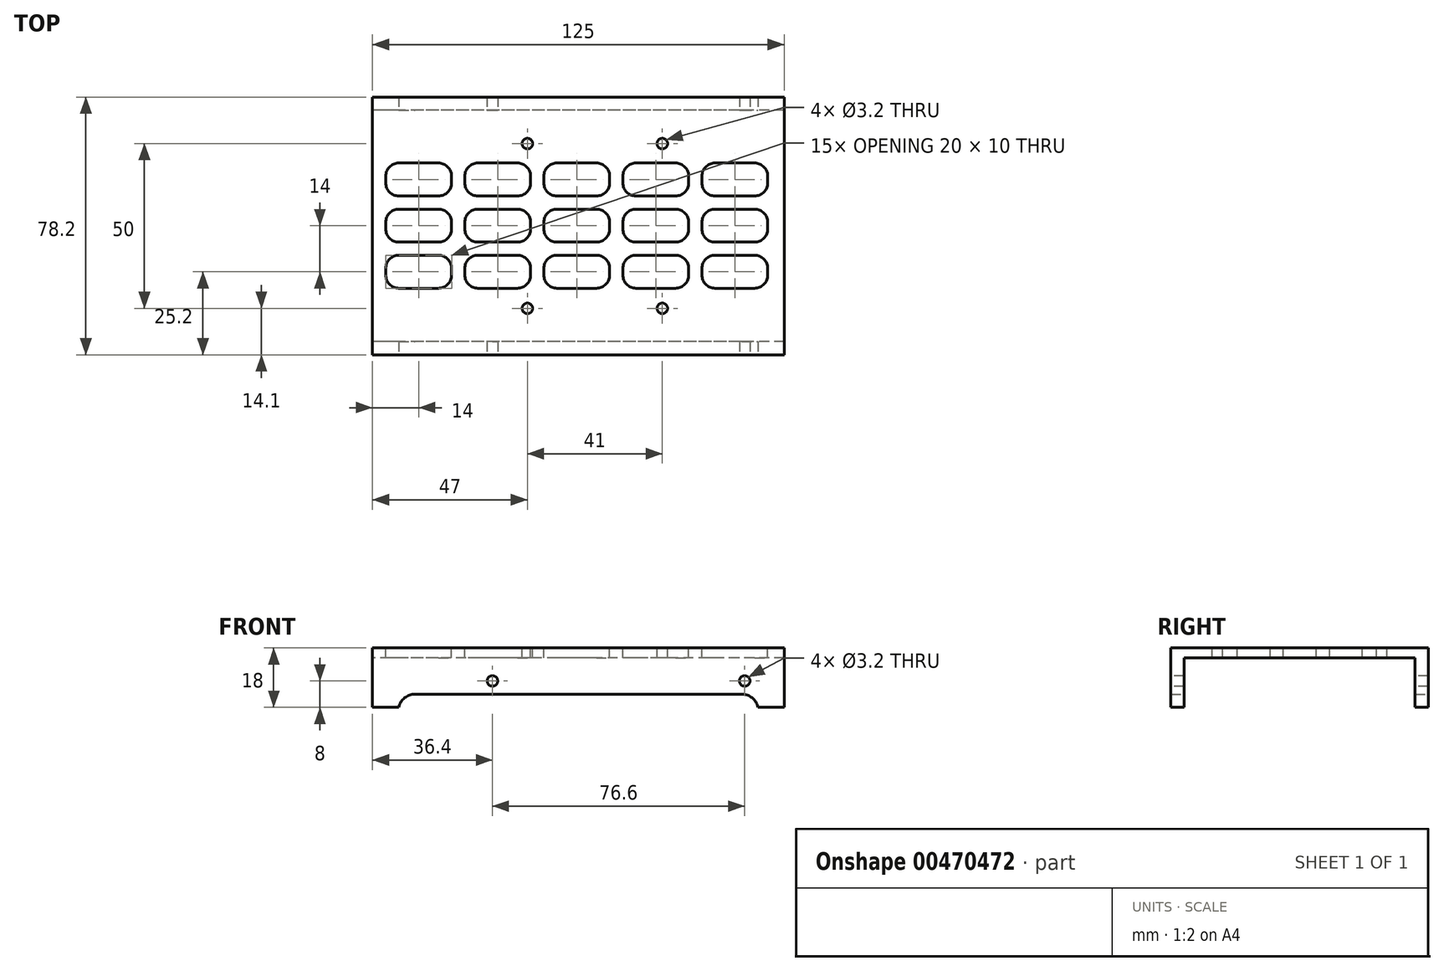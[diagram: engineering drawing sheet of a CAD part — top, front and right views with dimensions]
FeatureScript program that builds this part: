
annotation { "Feature Type Name" : "Feature", "Feature Type Description" : "" }
export const myFeature = defineFeature(function(context is Context, id is Id, definition is map)
    precondition{}
    {
        {
            var Q0;
            Q0=qCreatedBy(makeId("Top.planeOp"),FACE);
            var sketch = newSketch(context, id + "F0", { "sketchPlane" : qUnion([Q0])});
            skLineSegment(sketch, "E0.bottom", {"start": v(0, 0) * mm, "end": v(125, 0) * mm});
            skLineSegment(sketch, "E0.top", {"start": v(0, 78.2) * mm, "end": v(125, 78.2) * mm});
            skLineSegment(sketch, "E0.left", {"start": v(0, 0) * mm, "end": v(0, 78.2) * mm});
            skLineSegment(sketch, "E0.right", {"start": v(125, 0) * mm, "end": v(125, 78.2) * mm});
            skSolve(sketch);
        }
        {
            var Q0;
            Q0 = qSketchRegion(id + "F0", true);
            extrude(context, id + "F1", {"entities" : qUnion([Q0]), "depth" : 3 * mm});
        }
        {
            var Q0;
            Q0=makeQuery(id+"F1.opExtrude","CAP_FACE",FACE,{"disambiguationData":[OSD([sQuery(id+"F0.wireOp",EDGE,"E0.bottom"),sQuery(id+"F0.wireOp",EDGE,"E0.top"),sQuery(id+"F0.wireOp",EDGE,"E0.left"),sQuery(id+"F0.wireOp",EDGE,"E0.right")])],"isStart":true});
            var sketch = newSketch(context, id + "F2", { "sketchPlane" : qUnion([Q0])});
            skLineSegment(sketch, "E1.bottom", {"start": v(125, -78.2) * mm, "end": v(0, -78.2) * mm});
            skLineSegment(sketch, "E1.top", {"start": v(125, -74.2) * mm, "end": v(0, -74.2) * mm});
            skLineSegment(sketch, "E1.left", {"start": v(125, -78.2) * mm, "end": v(125, -74.2) * mm});
            skLineSegment(sketch, "E1.right", {"start": v(0, -78.2) * mm, "end": v(0, -74.2) * mm});
            skLineSegment(sketch, "E2.bottom", {"start": v(125, 0) * mm, "end": v(0, 0) * mm});
            skLineSegment(sketch, "E2.top", {"start": v(125, -4) * mm, "end": v(0, -4) * mm});
            skLineSegment(sketch, "E2.left", {"start": v(125, 0) * mm, "end": v(125, -4) * mm});
            skLineSegment(sketch, "E2.right", {"start": v(0, 0) * mm, "end": v(0, -4) * mm});
            skSolve(sketch);
        }
        {
            var Q0;
            Q0 = qSketchRegion(id + "F2", true);
            extrude(context, id + "F3", {"entities" : qUnion([Q0]), "operationType" : NewBodyOperationType.ADD, "depth" : 15 * mm});
        }
        {
            var Q0;
            Q0=makeQuery(id+"F3.boolean.opBoolean","MERGE",FACE,{"derivedFrom":[makeQuery(id+"F1.opExtrude","SWEPT_FACE",FACE,{"disambiguationData":[OSD([sQuery(id+"F0.wireOp",EDGE,"E0.bottom")])]}),makeQuery(id+"F3.opExtrude","SWEPT_FACE",FACE,{"disambiguationData":[OSD([sQuery(id+"F2.wireOp",EDGE,"E2.bottom")])]})]});
            var sketch = newSketch(context, id + "F4", { "sketchPlane" : qUnion([Q0])});
            skPoint(sketch, "E3", {"position": v(113, -7) * mm});
            skPoint(sketch, "E4.1.0.0", {"position": v(36.4, -7) * mm});
            skLineSegment(sketch, "E4.direction1", {"start": v(113, -7) * mm, "end": v(36.4, -7) * mm, "construction": true});
            skSolve(sketch);
        }
        {
            var Q0;
            Q0=sQuery(id+"F4.wireOp",VERTEX,"E3");
            var Q1;
            Q1=sQuery(id+"F4.wireOp",VERTEX,"E4.1.0.0");
            var Q2;
            Q2=makeQuery(id+"F1.opExtrude","SWEPT_BODY",BODY,{"disambiguationData":[OSD([sQuery(id+"F0.wireOp",EDGE,"E0.bottom"),sQuery(id+"F0.wireOp",EDGE,"E0.top"),sQuery(id+"F0.wireOp",EDGE,"E0.left"),sQuery(id+"F0.wireOp",EDGE,"E0.right")])]});
            hole(context, id + "F5", {"style" : HoleStyle.SIMPLE, "endStyle" : HoleEndStyle.THROUGH, "holeDiameter" : 3.2 * mm, "isTappedThrough" : true, "tappedDepth" : 12 * mm, "tapClearance" : 3, "locations" : qUnion([Q0, Q1]), "scope" : qUnion([Q2])});
        }
        {
            var Q0;
            Q0=makeQuery(id+"F3.boolean.opBoolean","MERGE",FACE,{"derivedFrom":[makeQuery(id+"F1.opExtrude","SWEPT_FACE",FACE,{"disambiguationData":[OSD([sQuery(id+"F0.wireOp",EDGE,"E0.bottom")])]}),makeQuery(id+"F3.opExtrude","SWEPT_FACE",FACE,{"disambiguationData":[OSD([sQuery(id+"F2.wireOp",EDGE,"E2.bottom")])]})]});
            var sketch = newSketch(context, id + "F6", { "sketchPlane" : qUnion([Q0])});
            skLineSegment(sketch, "E5.bottom", {"start": v(8, -11) * mm, "end": v(117, -11) * mm});
            skLineSegment(sketch, "E5.top", {"start": v(8, -15) * mm, "end": v(117, -15) * mm});
            skLineSegment(sketch, "E5.left", {"start": v(8, -11) * mm, "end": v(8, -15) * mm});
            skLineSegment(sketch, "E5.right", {"start": v(117, -11) * mm, "end": v(117, -15) * mm});
            skSolve(sketch);
        }
        {
            var Q0;
            Q0 = qSketchRegion(id + "F6", true);
            extrude(context, id + "F7", {"entities" : qUnion([Q0]), "operationType" : NewBodyOperationType.REMOVE, "endBound" : BoundingType.THROUGH_ALL, "oppositeDirection" : true, "depth" : 25 * mm});
        }
        {
            var Q0;
            Q0=makeQuery(id+"F1.opExtrude","CAP_FACE",FACE,{"disambiguationData":[OSD([sQuery(id+"F0.wireOp",EDGE,"E0.bottom"),sQuery(id+"F0.wireOp",EDGE,"E0.top"),sQuery(id+"F0.wireOp",EDGE,"E0.left"),sQuery(id+"F0.wireOp",EDGE,"E0.right")])],"isStart":false});
            var sketch = newSketch(context, id + "F8", { "sketchPlane" : qUnion([Q0])});
            skPoint(sketch, "E6", {"position": v(47, 64.1) * mm});
            skPoint(sketch, "E7.0.1.0", {"position": v(47, 14.1) * mm});
            skPoint(sketch, "E7.1.0.0", {"position": v(88, 64.1) * mm});
            skPoint(sketch, "E7.1.1.0", {"position": v(88, 14.1) * mm});
            skLineSegment(sketch, "E7.direction1", {"start": v(47, 64.1) * mm, "end": v(88, 64.1) * mm, "construction": true});
            skLineSegment(sketch, "E7.direction2", {"start": v(47, 64.1) * mm, "end": v(47, 14.1) * mm, "construction": true});
            skSolve(sketch);
        }
        {
            var Q0;
            Q0=sQuery(id+"F8.wireOp",VERTEX,"E7.0.1.0");
            var Q1;
            Q1=sQuery(id+"F8.wireOp",VERTEX,"E7.1.1.0");
            var Q2;
            Q2=sQuery(id+"F8.wireOp",VERTEX,"E7.1.0.0");
            var Q3;
            Q3=sQuery(id+"F8.wireOp",VERTEX,"E6");
            var Q4;
            Q4=makeQuery(id+"F1.opExtrude","SWEPT_BODY",BODY,{"disambiguationData":[OSD([sQuery(id+"F0.wireOp",EDGE,"E0.bottom"),sQuery(id+"F0.wireOp",EDGE,"E0.top"),sQuery(id+"F0.wireOp",EDGE,"E0.left"),sQuery(id+"F0.wireOp",EDGE,"E0.right")])]});
            hole(context, id + "F9", {"style" : HoleStyle.SIMPLE, "endStyle" : HoleEndStyle.THROUGH, "holeDiameter" : 3.2 * mm, "isTappedThrough" : true, "tappedDepth" : 12 * mm, "tapClearance" : 3, "locations" : qUnion([Q0, Q1, Q2, Q3]), "scope" : qUnion([Q4])});
        }
        {
            var Q0;
            {var subQ0=sQuery(id+"F6.wireOp",EDGE,"E5.bottom");var subQ1=sQuery(id+"F6.wireOp",EDGE,"E5.right");Q0=makeQuery(id+"F7.boolean.opBoolean","COPY",EDGE,{"disambiguationData":[TD([makeQuery(id+"F1.opExtrude","SWEPT_FACE",FACE,{"disambiguationData":[OSD([sQuery(id+"F0.wireOp",EDGE,"E0.bottom")])]})])],"derivedFrom":makeQuery(id+"F7.opExtrude","SWEPT_EDGE",EDGE,{"disambiguationData":[OSD([subQ0,subQ1])]})});}
            var Q1;
            {var subQ0=sQuery(id+"F6.wireOp",EDGE,"E5.bottom");var subQ1=sQuery(id+"F6.wireOp",EDGE,"E5.right");Q1=makeQuery(id+"F7.boolean.opBoolean","COPY",EDGE,{"disambiguationData":[TD([makeQuery(id+"F1.opExtrude","SWEPT_FACE",FACE,{"disambiguationData":[OSD([sQuery(id+"F0.wireOp",EDGE,"E0.top")])]})])],"derivedFrom":makeQuery(id+"F7.opExtrude","SWEPT_EDGE",EDGE,{"disambiguationData":[OSD([subQ0,subQ1])]})});}
            var Q2;
            {var subQ0=sQuery(id+"F6.wireOp",EDGE,"E5.bottom");var subQ1=sQuery(id+"F6.wireOp",EDGE,"E5.left");Q2=makeQuery(id+"F7.boolean.opBoolean","COPY",EDGE,{"disambiguationData":[TD([makeQuery(id+"F1.opExtrude","SWEPT_FACE",FACE,{"disambiguationData":[OSD([sQuery(id+"F0.wireOp",EDGE,"E0.bottom")])]})])],"derivedFrom":makeQuery(id+"F7.opExtrude","SWEPT_EDGE",EDGE,{"disambiguationData":[OSD([subQ0,subQ1])]})});}
            var Q3;
            {var subQ0=sQuery(id+"F6.wireOp",EDGE,"E5.bottom");var subQ1=sQuery(id+"F6.wireOp",EDGE,"E5.left");Q3=makeQuery(id+"F7.boolean.opBoolean","COPY",EDGE,{"disambiguationData":[TD([makeQuery(id+"F1.opExtrude","SWEPT_FACE",FACE,{"disambiguationData":[OSD([sQuery(id+"F0.wireOp",EDGE,"E0.top")])]})])],"derivedFrom":makeQuery(id+"F7.opExtrude","SWEPT_EDGE",EDGE,{"disambiguationData":[OSD([subQ0,subQ1])]})});}
            fillet(context, id + "F10", {"entities" : qUnion([Q0, Q1, Q2, Q3]), "radius" : 5 * mm, "tangentPropagation" : true, "allowEdgeOverflow" : false});
        }
        {
            var Q0;
            Q0=makeQuery(id+"F1.opExtrude","CAP_FACE",FACE,{"disambiguationData":[OSD([sQuery(id+"F0.wireOp",EDGE,"E0.bottom"),sQuery(id+"F0.wireOp",EDGE,"E0.top"),sQuery(id+"F0.wireOp",EDGE,"E0.left"),sQuery(id+"F0.wireOp",EDGE,"E0.right")])],"isStart":false});
            var sketch = newSketch(context, id + "F11", { "sketchPlane" : qUnion([Q0])});
            skLineSegment(sketch, "E8.bottom", {"start": v(8, 58.2) * mm, "end": v(20, 58.2) * mm});
            skLineSegment(sketch, "E8.top", {"start": v(8, 48.2) * mm, "end": v(20, 48.2) * mm});
            skLineSegment(sketch, "E8.left", {"start": v(4, 54.2) * mm, "end": v(4, 52.2) * mm});
            skLineSegment(sketch, "E8.right", {"start": v(24, 54.2) * mm, "end": v(24, 52.2) * mm});
            skPoint(sketch, "E9.visualSharp", {"position": v(4, 58.2) * mm});
            skArc(sketch, "E9.filletArc", {"start": v(8, 58.2) * mm, "mid": v(5.17, 57.03) * mm, "end": v(4, 54.2) * mm});
            skPoint(sketch, "E10.visualSharp", {"position": v(4, 48.2) * mm});
            skArc(sketch, "E10.filletArc", {"start": v(4, 52.2) * mm, "mid": v(5.17, 49.37) * mm, "end": v(8, 48.2) * mm});
            skPoint(sketch, "E11.visualSharp", {"position": v(24, 58.2) * mm});
            skArc(sketch, "E11.filletArc", {"start": v(24, 54.2) * mm, "mid": v(22.83, 57.03) * mm, "end": v(20, 58.2) * mm});
            skPoint(sketch, "E12.visualSharp", {"position": v(24, 48.2) * mm});
            skArc(sketch, "E12.filletArc", {"start": v(20, 48.2) * mm, "mid": v(22.83, 49.37) * mm, "end": v(24, 52.2) * mm});
            skArc(sketch, "E13.0.1.0", {"start": v(8, 44.2) * mm, "mid": v(5.17, 43.03) * mm, "end": v(4, 40.2) * mm});
            skLineSegment(sketch, "E13.0.1.1", {"start": v(4, 40.2) * mm, "end": v(4, 38.2) * mm});
            skArc(sketch, "E13.0.1.2", {"start": v(4, 38.2) * mm, "mid": v(5.17, 35.37) * mm, "end": v(8, 34.2) * mm});
            skLineSegment(sketch, "E13.0.1.3", {"start": v(8, 34.2) * mm, "end": v(20, 34.2) * mm});
            skArc(sketch, "E13.0.1.4", {"start": v(20, 34.2) * mm, "mid": v(22.83, 35.37) * mm, "end": v(24, 38.2) * mm});
            skLineSegment(sketch, "E13.0.1.5", {"start": v(24, 40.2) * mm, "end": v(24, 38.2) * mm});
            skArc(sketch, "E13.0.1.6", {"start": v(24, 40.2) * mm, "mid": v(22.83, 43.03) * mm, "end": v(20, 44.2) * mm});
            skLineSegment(sketch, "E13.0.1.7", {"start": v(8, 44.2) * mm, "end": v(20, 44.2) * mm});
            skArc(sketch, "E13.0.2.0", {"start": v(8, 30.2) * mm, "mid": v(5.17, 29.03) * mm, "end": v(4, 26.2) * mm});
            skLineSegment(sketch, "E13.0.2.1", {"start": v(4, 26.2) * mm, "end": v(4, 24.2) * mm});
            skArc(sketch, "E13.0.2.2", {"start": v(4, 24.2) * mm, "mid": v(5.17, 21.37) * mm, "end": v(8, 20.2) * mm});
            skLineSegment(sketch, "E13.0.2.3", {"start": v(8, 20.2) * mm, "end": v(20, 20.2) * mm});
            skArc(sketch, "E13.0.2.4", {"start": v(20, 20.2) * mm, "mid": v(22.83, 21.37) * mm, "end": v(24, 24.2) * mm});
            skLineSegment(sketch, "E13.0.2.5", {"start": v(24, 26.2) * mm, "end": v(24, 24.2) * mm});
            skArc(sketch, "E13.0.2.6", {"start": v(24, 26.2) * mm, "mid": v(22.83, 29.03) * mm, "end": v(20, 30.2) * mm});
            skLineSegment(sketch, "E13.0.2.7", {"start": v(8, 30.2) * mm, "end": v(20, 30.2) * mm});
            skArc(sketch, "E13.1.0.0", {"start": v(32, 58.2) * mm, "mid": v(29.17, 57.03) * mm, "end": v(28, 54.2) * mm});
            skLineSegment(sketch, "E13.1.0.1", {"start": v(28, 54.2) * mm, "end": v(28, 52.2) * mm});
            skArc(sketch, "E13.1.0.2", {"start": v(28, 52.2) * mm, "mid": v(29.17, 49.37) * mm, "end": v(32, 48.2) * mm});
            skLineSegment(sketch, "E13.1.0.3", {"start": v(32, 48.2) * mm, "end": v(44, 48.2) * mm});
            skArc(sketch, "E13.1.0.4", {"start": v(44, 48.2) * mm, "mid": v(46.83, 49.37) * mm, "end": v(48, 52.2) * mm});
            skLineSegment(sketch, "E13.1.0.5", {"start": v(48, 54.2) * mm, "end": v(48, 52.2) * mm});
            skArc(sketch, "E13.1.0.6", {"start": v(48, 54.2) * mm, "mid": v(46.83, 57.03) * mm, "end": v(44, 58.2) * mm});
            skLineSegment(sketch, "E13.1.0.7", {"start": v(32, 58.2) * mm, "end": v(44, 58.2) * mm});
            skArc(sketch, "E13.1.1.0", {"start": v(32, 44.2) * mm, "mid": v(29.17, 43.03) * mm, "end": v(28, 40.2) * mm});
            skLineSegment(sketch, "E13.1.1.1", {"start": v(28, 40.2) * mm, "end": v(28, 38.2) * mm});
            skArc(sketch, "E13.1.1.2", {"start": v(28, 38.2) * mm, "mid": v(29.17, 35.37) * mm, "end": v(32, 34.2) * mm});
            skLineSegment(sketch, "E13.1.1.3", {"start": v(32, 34.2) * mm, "end": v(44, 34.2) * mm});
            skArc(sketch, "E13.1.1.4", {"start": v(44, 34.2) * mm, "mid": v(46.83, 35.37) * mm, "end": v(48, 38.2) * mm});
            skLineSegment(sketch, "E13.1.1.5", {"start": v(48, 40.2) * mm, "end": v(48, 38.2) * mm});
            skArc(sketch, "E13.1.1.6", {"start": v(48, 40.2) * mm, "mid": v(46.83, 43.03) * mm, "end": v(44, 44.2) * mm});
            skLineSegment(sketch, "E13.1.1.7", {"start": v(32, 44.2) * mm, "end": v(44, 44.2) * mm});
            skArc(sketch, "E13.1.2.0", {"start": v(32, 30.2) * mm, "mid": v(29.17, 29.03) * mm, "end": v(28, 26.2) * mm});
            skLineSegment(sketch, "E13.1.2.1", {"start": v(28, 26.2) * mm, "end": v(28, 24.2) * mm});
            skArc(sketch, "E13.1.2.2", {"start": v(28, 24.2) * mm, "mid": v(29.17, 21.37) * mm, "end": v(32, 20.2) * mm});
            skLineSegment(sketch, "E13.1.2.3", {"start": v(32, 20.2) * mm, "end": v(44, 20.2) * mm});
            skArc(sketch, "E13.1.2.4", {"start": v(44, 20.2) * mm, "mid": v(46.83, 21.37) * mm, "end": v(48, 24.2) * mm});
            skLineSegment(sketch, "E13.1.2.5", {"start": v(48, 26.2) * mm, "end": v(48, 24.2) * mm});
            skArc(sketch, "E13.1.2.6", {"start": v(48, 26.2) * mm, "mid": v(46.83, 29.03) * mm, "end": v(44, 30.2) * mm});
            skLineSegment(sketch, "E13.1.2.7", {"start": v(32, 30.2) * mm, "end": v(44, 30.2) * mm});
            skArc(sketch, "E13.2.0.0", {"start": v(56, 58.2) * mm, "mid": v(53.17, 57.03) * mm, "end": v(52, 54.2) * mm});
            skLineSegment(sketch, "E13.2.0.1", {"start": v(52, 54.2) * mm, "end": v(52, 52.2) * mm});
            skArc(sketch, "E13.2.0.2", {"start": v(52, 52.2) * mm, "mid": v(53.17, 49.37) * mm, "end": v(56, 48.2) * mm});
            skLineSegment(sketch, "E13.2.0.3", {"start": v(56, 48.2) * mm, "end": v(68, 48.2) * mm});
            skArc(sketch, "E13.2.0.4", {"start": v(68, 48.2) * mm, "mid": v(70.83, 49.37) * mm, "end": v(72, 52.2) * mm});
            skLineSegment(sketch, "E13.2.0.5", {"start": v(72, 54.2) * mm, "end": v(72, 52.2) * mm});
            skArc(sketch, "E13.2.0.6", {"start": v(72, 54.2) * mm, "mid": v(70.83, 57.03) * mm, "end": v(68, 58.2) * mm});
            skLineSegment(sketch, "E13.2.0.7", {"start": v(56, 58.2) * mm, "end": v(68, 58.2) * mm});
            skArc(sketch, "E13.2.1.0", {"start": v(56, 44.2) * mm, "mid": v(53.17, 43.03) * mm, "end": v(52, 40.2) * mm});
            skLineSegment(sketch, "E13.2.1.1", {"start": v(52, 40.2) * mm, "end": v(52, 38.2) * mm});
            skArc(sketch, "E13.2.1.2", {"start": v(52, 38.2) * mm, "mid": v(53.17, 35.37) * mm, "end": v(56, 34.2) * mm});
            skLineSegment(sketch, "E13.2.1.3", {"start": v(56, 34.2) * mm, "end": v(68, 34.2) * mm});
            skArc(sketch, "E13.2.1.4", {"start": v(68, 34.2) * mm, "mid": v(70.83, 35.37) * mm, "end": v(72, 38.2) * mm});
            skLineSegment(sketch, "E13.2.1.5", {"start": v(72, 40.2) * mm, "end": v(72, 38.2) * mm});
            skArc(sketch, "E13.2.1.6", {"start": v(72, 40.2) * mm, "mid": v(70.83, 43.03) * mm, "end": v(68, 44.2) * mm});
            skLineSegment(sketch, "E13.2.1.7", {"start": v(56, 44.2) * mm, "end": v(68, 44.2) * mm});
            skArc(sketch, "E13.2.2.0", {"start": v(56, 30.2) * mm, "mid": v(53.17, 29.03) * mm, "end": v(52, 26.2) * mm});
            skLineSegment(sketch, "E13.2.2.1", {"start": v(52, 26.2) * mm, "end": v(52, 24.2) * mm});
            skArc(sketch, "E13.2.2.2", {"start": v(52, 24.2) * mm, "mid": v(53.17, 21.37) * mm, "end": v(56, 20.2) * mm});
            skLineSegment(sketch, "E13.2.2.3", {"start": v(56, 20.2) * mm, "end": v(68, 20.2) * mm});
            skArc(sketch, "E13.2.2.4", {"start": v(68, 20.2) * mm, "mid": v(70.83, 21.37) * mm, "end": v(72, 24.2) * mm});
            skLineSegment(sketch, "E13.2.2.5", {"start": v(72, 26.2) * mm, "end": v(72, 24.2) * mm});
            skArc(sketch, "E13.2.2.6", {"start": v(72, 26.2) * mm, "mid": v(70.83, 29.03) * mm, "end": v(68, 30.2) * mm});
            skLineSegment(sketch, "E13.2.2.7", {"start": v(56, 30.2) * mm, "end": v(68, 30.2) * mm});
            skLineSegment(sketch, "E13.direction1", {"start": v(8, 48.2) * mm, "end": v(32, 48.2) * mm, "construction": true});
            skLineSegment(sketch, "E13.direction2", {"start": v(8, 48.2) * mm, "end": v(8, 34.2) * mm, "construction": true});
            skArc(sketch, "E14.0.3.0", {"start": v(80, 58.2) * mm, "mid": v(77.17, 57.03) * mm, "end": v(76, 54.2) * mm});
            skLineSegment(sketch, "E14.4.3.0", {"start": v(76, 54.2) * mm, "end": v(76, 52.2) * mm});
            skArc(sketch, "E14.7.3.0", {"start": v(76, 52.2) * mm, "mid": v(77.17, 49.37) * mm, "end": v(80, 48.2) * mm});
            skLineSegment(sketch, "E14.11.3.0", {"start": v(80, 48.2) * mm, "end": v(92, 48.2) * mm});
            skArc(sketch, "E14.14.3.0", {"start": v(92, 48.2) * mm, "mid": v(94.83, 49.37) * mm, "end": v(96, 52.2) * mm});
            skLineSegment(sketch, "E14.18.3.0", {"start": v(96, 54.2) * mm, "end": v(96, 52.2) * mm});
            skArc(sketch, "E14.21.3.0", {"start": v(96, 54.2) * mm, "mid": v(94.83, 57.03) * mm, "end": v(92, 58.2) * mm});
            skLineSegment(sketch, "E14.25.3.0", {"start": v(80, 58.2) * mm, "end": v(92, 58.2) * mm});
            skArc(sketch, "E14.0.3.1", {"start": v(80, 44.2) * mm, "mid": v(77.17, 43.03) * mm, "end": v(76, 40.2) * mm});
            skLineSegment(sketch, "E14.4.3.1", {"start": v(76, 40.2) * mm, "end": v(76, 38.2) * mm});
            skArc(sketch, "E14.7.3.1", {"start": v(76, 38.2) * mm, "mid": v(77.17, 35.37) * mm, "end": v(80, 34.2) * mm});
            skLineSegment(sketch, "E14.11.3.1", {"start": v(80, 34.2) * mm, "end": v(92, 34.2) * mm});
            skArc(sketch, "E14.14.3.1", {"start": v(92, 34.2) * mm, "mid": v(94.83, 35.37) * mm, "end": v(96, 38.2) * mm});
            skLineSegment(sketch, "E14.18.3.1", {"start": v(96, 40.2) * mm, "end": v(96, 38.2) * mm});
            skArc(sketch, "E14.21.3.1", {"start": v(96, 40.2) * mm, "mid": v(94.83, 43.03) * mm, "end": v(92, 44.2) * mm});
            skLineSegment(sketch, "E14.25.3.1", {"start": v(80, 44.2) * mm, "end": v(92, 44.2) * mm});
            skArc(sketch, "E14.0.3.2", {"start": v(80, 30.2) * mm, "mid": v(77.17, 29.03) * mm, "end": v(76, 26.2) * mm});
            skLineSegment(sketch, "E14.4.3.2", {"start": v(76, 26.2) * mm, "end": v(76, 24.2) * mm});
            skArc(sketch, "E14.7.3.2", {"start": v(76, 24.2) * mm, "mid": v(77.17, 21.37) * mm, "end": v(80, 20.2) * mm});
            skLineSegment(sketch, "E14.11.3.2", {"start": v(80, 20.2) * mm, "end": v(92, 20.2) * mm});
            skArc(sketch, "E14.14.3.2", {"start": v(92, 20.2) * mm, "mid": v(94.83, 21.37) * mm, "end": v(96, 24.2) * mm});
            skLineSegment(sketch, "E14.18.3.2", {"start": v(96, 26.2) * mm, "end": v(96, 24.2) * mm});
            skArc(sketch, "E14.21.3.2", {"start": v(96, 26.2) * mm, "mid": v(94.83, 29.03) * mm, "end": v(92, 30.2) * mm});
            skLineSegment(sketch, "E14.25.3.2", {"start": v(80, 30.2) * mm, "end": v(92, 30.2) * mm});
            skArc(sketch, "E14.0.4.0", {"start": v(104, 58.2) * mm, "mid": v(101.17, 57.03) * mm, "end": v(100, 54.2) * mm});
            skLineSegment(sketch, "E14.4.4.0", {"start": v(100, 54.2) * mm, "end": v(100, 52.2) * mm});
            skArc(sketch, "E14.7.4.0", {"start": v(100, 52.2) * mm, "mid": v(101.17, 49.37) * mm, "end": v(104, 48.2) * mm});
            skLineSegment(sketch, "E14.11.4.0", {"start": v(104, 48.2) * mm, "end": v(116, 48.2) * mm});
            skArc(sketch, "E14.14.4.0", {"start": v(116, 48.2) * mm, "mid": v(118.83, 49.37) * mm, "end": v(120, 52.2) * mm});
            skLineSegment(sketch, "E14.18.4.0", {"start": v(120, 54.2) * mm, "end": v(120, 52.2) * mm});
            skArc(sketch, "E14.21.4.0", {"start": v(120, 54.2) * mm, "mid": v(118.83, 57.03) * mm, "end": v(116, 58.2) * mm});
            skLineSegment(sketch, "E14.25.4.0", {"start": v(104, 58.2) * mm, "end": v(116, 58.2) * mm});
            skArc(sketch, "E14.0.4.1", {"start": v(104, 44.2) * mm, "mid": v(101.17, 43.03) * mm, "end": v(100, 40.2) * mm});
            skLineSegment(sketch, "E14.4.4.1", {"start": v(100, 40.2) * mm, "end": v(100, 38.2) * mm});
            skArc(sketch, "E14.7.4.1", {"start": v(100, 38.2) * mm, "mid": v(101.17, 35.37) * mm, "end": v(104, 34.2) * mm});
            skLineSegment(sketch, "E14.11.4.1", {"start": v(104, 34.2) * mm, "end": v(116, 34.2) * mm});
            skArc(sketch, "E14.14.4.1", {"start": v(116, 34.2) * mm, "mid": v(118.83, 35.37) * mm, "end": v(120, 38.2) * mm});
            skLineSegment(sketch, "E14.18.4.1", {"start": v(120, 40.2) * mm, "end": v(120, 38.2) * mm});
            skArc(sketch, "E14.21.4.1", {"start": v(120, 40.2) * mm, "mid": v(118.83, 43.03) * mm, "end": v(116, 44.2) * mm});
            skLineSegment(sketch, "E14.25.4.1", {"start": v(104, 44.2) * mm, "end": v(116, 44.2) * mm});
            skArc(sketch, "E14.0.4.2", {"start": v(104, 30.2) * mm, "mid": v(101.17, 29.03) * mm, "end": v(100, 26.2) * mm});
            skLineSegment(sketch, "E14.4.4.2", {"start": v(100, 26.2) * mm, "end": v(100, 24.2) * mm});
            skArc(sketch, "E14.7.4.2", {"start": v(100, 24.2) * mm, "mid": v(101.17, 21.37) * mm, "end": v(104, 20.2) * mm});
            skLineSegment(sketch, "E14.11.4.2", {"start": v(104, 20.2) * mm, "end": v(116, 20.2) * mm});
            skArc(sketch, "E14.14.4.2", {"start": v(116, 20.2) * mm, "mid": v(118.83, 21.37) * mm, "end": v(120, 24.2) * mm});
            skLineSegment(sketch, "E14.18.4.2", {"start": v(120, 26.2) * mm, "end": v(120, 24.2) * mm});
            skArc(sketch, "E14.21.4.2", {"start": v(120, 26.2) * mm, "mid": v(118.83, 29.03) * mm, "end": v(116, 30.2) * mm});
            skLineSegment(sketch, "E14.25.4.2", {"start": v(104, 30.2) * mm, "end": v(116, 30.2) * mm});
            skSolve(sketch);
        }
        {
            var Q0;
            Q0 = qSketchRegion(id + "F11", true);
            extrude(context, id + "F12", {"entities" : qUnion([Q0]), "operationType" : NewBodyOperationType.REMOVE, "endBound" : BoundingType.UP_TO_NEXT, "oppositeDirection" : true, "depth" : 25 * mm});
        }
    });
